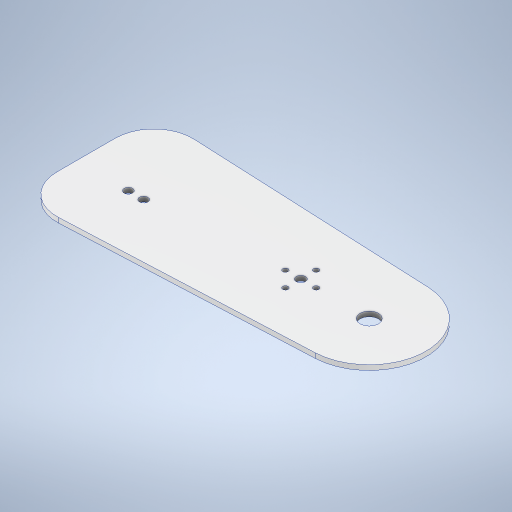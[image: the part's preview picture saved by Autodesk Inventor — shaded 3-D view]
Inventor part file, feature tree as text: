
AUTODESK INVENTOR PART (.ipt)
format: ipt  version: 2023 (Build 270158030, 158C)  size: 270,848 bytes
history: native  units: in
note: dims shown in document units (in); Inventor stores cm internally (conversion verified against a paired STEP export)
features: extrude x4, sketch x3
ambient origin geometry x8: Origin, YZ Plane, XZ Plane, XY Plane, X Axis, Y Axis, Z Axis, Center Point
bodies: Solid1 (feature_tree)
feature tree (7):
  extrude  "Main"  Depth=6.2598in
  extrude  "Axis Holes"  Depth=1.45in
  extrude  "Extrusion6"  Depth=0.2362in
  extrude  "Extrusion8"  TaperAngle=0.0deg  [1 undecoded]
  sketch  "Sketch1"  dims[d0=1.9685in d1=6.2598in]
  sketch  "Sketch5"  dims[d2=1.5in d3=1.45in]
  sketch  "Sketch7"  dims[d4=0.125in d5=0.0in d6=0.2362in d7=0.0in d8=0.0in d40=0.4724in d41=1.751in d43=2.0in d44=0.2756in d45=0.3937in d46=0.2165in d47=0.0in d48=0.0in d58=0.1378in d59=1.5748in d61=360.0deg d63=0.7874in d64=0.3937in d65=0.0in]
note: 1 required parameter value undecoded (feature->parameter linkage not recoverable at this tier; creation-order binding heuristic only, values carry confidence <= 0.55)
